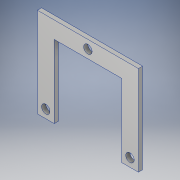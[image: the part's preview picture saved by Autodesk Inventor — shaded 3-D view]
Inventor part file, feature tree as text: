
AUTODESK INVENTOR PART (.ipt)
format: ipt  version: 2018.1 (Build 221171000, 171)  size: 121,344 bytes
history: native  units: mm
features: extrude x2, sketch x2, other x1
ambient origin geometry x8: Origin, YZ Plane, XZ Plane, XY Plane, X Axis, Y Axis, Z Axis, Center Point
bodies: Body1 (feature_tree)
feature tree (5):
  other  "ソリッド1"
  extrude  "押し出し1"  Depth=20.0mm
  extrude  "押し出し2"  Depth=20.0mm
  sketch  "スケッチ1"
  sketch  "スケッチ2"
